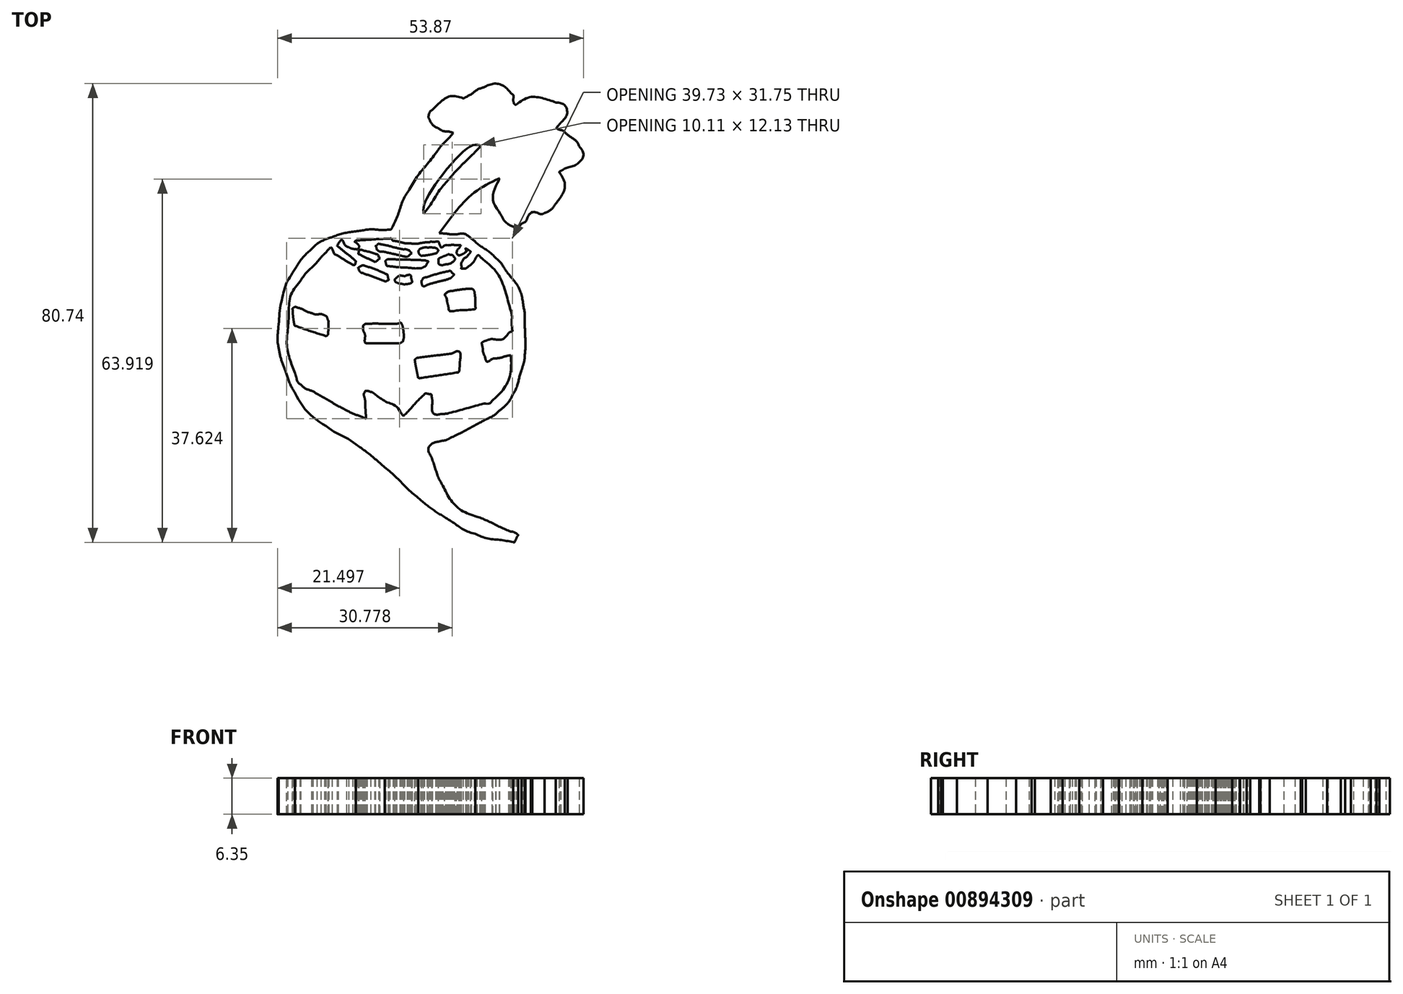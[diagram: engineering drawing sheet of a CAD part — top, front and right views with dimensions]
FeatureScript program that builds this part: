
annotation { "Feature Type Name" : "Feature", "Feature Type Description" : "" }
export const myFeature = defineFeature(function(context is Context, id is Id, definition is map)
    precondition{}
    {
        {
            var Q0;
            Q0=qCreatedBy(makeId("Top.planeOp"),FACE);
            var sketch = newSketch(context, id + "F0", { "sketchPlane" : qUnion([Q0])});
            skFitSpline(sketch, "E0", {"points": [v(4.2, 31.85) * mm, v(3.38, 32.06) * mm, v(2.48, 32.16) * mm, v(1.72, 32.55) * mm]});
            skFitSpline(sketch, "E1", {"points": [v(1.72, 32.55) * mm, v(1.05, 32.89) * mm, v(0.37, 33.47) * mm, v(0.05, 34.12) * mm]});
            skFitSpline(sketch, "E2", {"points": [v(0.05, 34.12) * mm, v(-0.16, 34.54) * mm, v(0.06, 35.5) * mm, v(0.43, 35.84) * mm]});
            skFitSpline(sketch, "E3", {"points": [v(0.43, 35.84) * mm, v(1.95, 37.26) * mm, v(3.7, 38.3) * mm, v(5.93, 37.94) * mm]});
            skFitSpline(sketch, "E4", {"points": [v(5.93, 37.94) * mm, v(6.07, 37.92) * mm, v(6.23, 38.06) * mm, v(6.37, 38.13) * mm]});
            skFitSpline(sketch, "E5", {"points": [v(6.37, 38.13) * mm, v(7.43, 38.71) * mm, v(8.44, 39.44) * mm, v(9.56, 39.85) * mm]});
            skFitSpline(sketch, "E6", {"points": [v(9.56, 39.85) * mm, v(11.38, 40.5) * mm, v(13.1, 40.04) * mm, v(14.48, 38.7) * mm]});
            skFitSpline(sketch, "E7", {"points": [v(14.48, 38.7) * mm, v(14.82, 38.38) * mm, v(14.73, 37.63) * mm, v(14.88, 37.09) * mm]});
            skFitSpline(sketch, "E8", {"points": [v(14.88, 37.09) * mm, v(14.92, 36.96) * mm, v(15.2, 36.77) * mm, v(15.27, 36.8) * mm]});
            skFitSpline(sketch, "E9", {"points": [v(15.27, 36.8) * mm, v(17.56, 38.1) * mm, v(19.92, 37.93) * mm, v(22.3, 37.18) * mm]});
            skFitSpline(sketch, "E10", {"points": [v(22.3, 37.18) * mm, v(23.8, 36.71) * mm, v(24.18, 35.06) * mm, v(23.12, 33.67) * mm]});
            skFitSpline(sketch, "E11", {"points": [v(23.12, 33.67) * mm, v(22.87, 33.34) * mm, v(22.6, 33.03) * mm, v(22.3, 32.68) * mm]});
            skFitSpline(sketch, "E12", {"points": [v(22.3, 32.68) * mm, v(22.85, 32.41) * mm, v(23.45, 32.26) * mm, v(23.9, 31.9) * mm]});
            skFitSpline(sketch, "E13", {"points": [v(23.9, 31.9) * mm, v(24.77, 31.17) * mm, v(25.8, 30.46) * mm, v(26.32, 29.5) * mm]});
            skFitSpline(sketch, "E14", {"points": [v(26.32, 29.5) * mm, v(27.12, 28.07) * mm, v(26.07, 26.4) * mm, v(24.3, 25.73) * mm]});
            skFitSpline(sketch, "E15", {"points": [v(24.3, 25.73) * mm, v(23.84, 25.56) * mm, v(23.4, 25.3) * mm, v(22.97, 25.08) * mm]});
            skFitSpline(sketch, "E16", {"points": [v(22.97, 25.08) * mm, v(22.92, 25.05) * mm, v(22.87, 24.9) * mm, v(22.9, 24.83) * mm]});
            skFitSpline(sketch, "E17", {"points": [v(22.9, 24.83) * mm, v(23.83, 22.88) * mm, v(23.4, 21.04) * mm, v(22.24, 19.39) * mm]});
            skFitSpline(sketch, "E18", {"points": [v(22.24, 19.39) * mm, v(21.76, 18.7) * mm, v(21.01, 18.06) * mm, v(20.25, 17.75) * mm]});
            skFitSpline(sketch, "E19", {"points": [v(20.25, 17.75) * mm, v(19.66, 17.51) * mm, v(18.85, 17.83) * mm, v(18.13, 17.89) * mm]});
            skFitSpline(sketch, "E20", {"points": [v(18.13, 17.89) * mm, v(18.04, 17.9) * mm, v(17.9, 17.82) * mm, v(17.84, 17.75) * mm]});
            skFitSpline(sketch, "E21", {"points": [v(17.84, 17.75) * mm, v(17.34, 17.13) * mm, v(16.98, 16.3) * mm, v(16.34, 15.94) * mm]});
            skFitSpline(sketch, "E22", {"points": [v(16.34, 15.94) * mm, v(15.19, 15.3) * mm, v(13.33, 16.2) * mm, v(12.56, 17.46) * mm, v(11.35, 19.41) * mm, v(11.29, 21.4) * mm, v(12.18, 23.47) * mm]});
            skFitSpline(sketch, "E23", {"points": [v(12.18, 23.47) * mm, v(12.23, 23.57) * mm, v(12.25, 23.67) * mm, v(12.3, 23.84) * mm]});
            skFitSpline(sketch, "E24", {"points": [v(12.3, 23.84) * mm, v(8.03, 21.44) * mm, v(4.7, 18.12) * mm, v(1.72, 14.17) * mm]});
            skFitSpline(sketch, "E25", {"points": [v(1.72, 14.17) * mm, v(2.9, 14.1) * mm, v(3.9, 13.97) * mm, v(4.9, 14.01) * mm]});
            skFitSpline(sketch, "E26", {"points": [v(4.9, 14.01) * mm, v(6.16, 14.07) * mm, v(7.07, 13.5) * mm, v(7.98, 12.76) * mm]});
            skFitSpline(sketch, "E27", {"points": [v(7.98, 12.76) * mm, v(9.19, 11.77) * mm, v(10.52, 10.92) * mm, v(11.64, 9.84) * mm]});
            skFitSpline(sketch, "E28", {"points": [v(11.64, 9.84) * mm, v(12.63, 8.88) * mm, v(13.4, 7.68) * mm, v(14.25, 6.58) * mm]});
            skFitSpline(sketch, "E29", {"points": [v(14.25, 6.58) * mm, v(15.44, 5.05) * mm, v(16.2, 3.3) * mm, v(16.52, 1.4) * mm]});
            skFitSpline(sketch, "E30", {"points": [v(16.52, 1.4) * mm, v(16.77, -0.04) * mm, v(16.78, -1.54) * mm, v(16.82, -3.02) * mm]});
            skFitSpline(sketch, "E31", {"points": [v(16.82, -3.02) * mm, v(16.87, -4.4) * mm, v(16.89, -5.79) * mm, v(16.78, -7.16) * mm]});
            skFitSpline(sketch, "E32", {"points": [v(16.78, -7.16) * mm, v(16.71, -8.11) * mm, v(16.47, -9.06) * mm, v(16.2, -9.98) * mm]});
            skFitSpline(sketch, "E33", {"points": [v(16.2, -9.98) * mm, v(15.76, -11.4) * mm, v(15.38, -12.87) * mm, v(14.69, -14.17) * mm]});
            skFitSpline(sketch, "E34", {"points": [v(14.69, -14.17) * mm, v(14.1, -15.26) * mm, v(13.24, -16.28) * mm, v(12.28, -17.08) * mm]});
            skFitSpline(sketch, "E35", {"points": [v(12.28, -17.08) * mm, v(11.27, -17.94) * mm, v(10.02, -18.55) * mm, v(8.84, -19.19) * mm]});
            skFitSpline(sketch, "E36", {"points": [v(8.84, -19.19) * mm, v(7.07, -20.15) * mm, v(5.27, -21.07) * mm, v(3.46, -21.95) * mm]});
            skFitSpline(sketch, "E37", {"points": [v(3.46, -21.95) * mm, v(2.89, -22.23) * mm, v(2.22, -22.34) * mm, v(1.6, -22.5) * mm]});
            skFitSpline(sketch, "E38", {"points": [v(1.6, -22.5) * mm, v(0.62, -22.77) * mm, v(-0.2, -23.7) * mm, v(0.36, -25.28) * mm]});
            skFitSpline(sketch, "E39", {"points": [v(0.36, -25.28) * mm, v(0.95, -26.96) * mm, v(1.52, -28.69) * mm, v(2.37, -30.25) * mm]});
            skFitSpline(sketch, "E40", {"points": [v(2.37, -30.25) * mm, v(3.71, -32.74) * mm, v(5.69, -34.62) * mm, v(8.39, -35.7) * mm]});
            skFitSpline(sketch, "E41", {"points": [v(8.39, -35.7) * mm, v(10.25, -36.45) * mm, v(12.06, -37.35) * mm, v(13.9, -38.16) * mm]});
            skFitSpline(sketch, "E42", {"points": [v(13.9, -38.16) * mm, v(14.23, -38.3) * mm, v(14.62, -38.33) * mm, v(14.95, -38.48) * mm]});
            skFitSpline(sketch, "E43", {"points": [v(14.95, -38.48) * mm, v(15.2, -38.6) * mm, v(15.61, -38.96) * mm, v(15.6, -39) * mm]});
            skFitSpline(sketch, "E44", {"points": [v(15.6, -39) * mm, v(15.33, -39.43) * mm, v(14.94, -40.21) * mm, v(14.71, -40.17) * mm]});
            skFitSpline(sketch, "E45", {"points": [v(14.71, -40.17) * mm, v(12.47, -39.8) * mm, v(10.17, -39.52) * mm, v(8.06, -38.74) * mm]});
            skFitSpline(sketch, "E46", {"points": [v(8.06, -38.74) * mm, v(6.06, -38) * mm, v(4.23, -36.78) * mm, v(2.4, -35.63) * mm]});
            skFitSpline(sketch, "E47", {"points": [v(2.4, -35.63) * mm, v(0.88, -34.66) * mm, v(-0.6, -33.58) * mm, v(-1.96, -32.4) * mm]});
            skFitSpline(sketch, "E48", {"points": [v(-1.96, -32.4) * mm, v(-3.99, -30.68) * mm, v(-5.86, -28.77) * mm, v(-7.87, -27.02) * mm]});
            skFitSpline(sketch, "E49", {"points": [v(-7.87, -27.02) * mm, v(-9.5, -25.6) * mm, v(-11.18, -24.23) * mm, v(-12.94, -23) * mm]});
            skFitSpline(sketch, "E50", {"points": [v(-12.94, -23) * mm, v(-14.54, -21.87) * mm, v(-16.33, -21.03) * mm, v(-17.94, -19.94) * mm, v(-20.27, -18.35) * mm, v(-22.24, -16.36) * mm, v(-23.66, -13.91) * mm]});
            skFitSpline(sketch, "E51", {"points": [v(-23.66, -13.91) * mm, v(-24.42, -12.6) * mm, v(-24.97, -11.17) * mm, v(-25.5, -9.74) * mm]});
            skFitSpline(sketch, "E52", {"points": [v(-25.5, -9.74) * mm, v(-25.95, -8.5) * mm, v(-26.33, -7.22) * mm, v(-26.55, -5.92) * mm]});
            skFitSpline(sketch, "E53", {"points": [v(-26.55, -5.92) * mm, v(-26.73, -4.9) * mm, v(-26.72, -3.83) * mm, v(-26.63, -2.8) * mm]});
            skFitSpline(sketch, "E54", {"points": [v(-26.63, -2.8) * mm, v(-26.45, -0.88) * mm, v(-26.3, 1.07) * mm, v(-25.87, 2.94) * mm, v(-25.52, 4.4) * mm, v(-24.9, 5.88) * mm, v(-24.12, 7.16) * mm]});
            skFitSpline(sketch, "E55", {"points": [v(-24.12, 7.16) * mm, v(-23.18, 8.69) * mm, v(-22.06, 10.16) * mm, v(-20.76, 11.38) * mm]});
            skFitSpline(sketch, "E56", {"points": [v(-20.76, 11.38) * mm, v(-19.76, 12.32) * mm, v(-18.44, 13.05) * mm, v(-17.14, 13.5) * mm]});
            skFitSpline(sketch, "E57", {"points": [v(-17.14, 13.5) * mm, v(-15.43, 14.1) * mm, v(-13.6, 14.44) * mm, v(-11.8, 14.67) * mm]});
            skFitSpline(sketch, "E58", {"points": [v(-11.8, 14.67) * mm, v(-10.21, 14.87) * mm, v(-8.59, 14.75) * mm, v(-6.98, 14.83) * mm]});
            skFitSpline(sketch, "E59", {"points": [v(-6.98, 14.83) * mm, v(-6.78, 14.84) * mm, v(-6.55, 15.22) * mm, v(-6.43, 15.48) * mm]});
            skFitSpline(sketch, "E60", {"points": [v(-6.43, 15.48) * mm, v(-5.47, 17.6) * mm, v(-4.73, 19.86) * mm, v(-3.54, 21.84) * mm]});
            skFitSpline(sketch, "E61", {"points": [v(-3.54, 21.84) * mm, v(-2.08, 24.26) * mm, v(-0.28, 26.47) * mm, v(1.44, 28.72) * mm]});
            skFitSpline(sketch, "E62", {"points": [v(1.44, 28.72) * mm, v(2.28, 29.82) * mm, v(3.28, 30.81) * mm, v(4.2, 31.85) * mm]});
            skFitSpline(sketch, "E63", {"points": [v(5.54, 12.07) * mm, v(4.84, 12.07) * mm, v(4.03, 12.12) * mm, v(3.24, 12.05) * mm]});
            skFitSpline(sketch, "E64", {"points": [v(3.24, 12.05) * mm, v(2.65, 12) * mm, v(2.1, 11.66) * mm, v(1.7, 12.48) * mm]});
            skFitSpline(sketch, "E65", {"points": [v(1.7, 12.48) * mm, v(1.57, 12.72) * mm, v(0.82, 12.64) * mm, v(0.36, 12.7) * mm]});
            skFitSpline(sketch, "E66", {"points": [v(0.36, 12.7) * mm, v(0.22, 12.7) * mm, v(0.08, 12.63) * mm, v(-0.07, 12.62) * mm]});
            skFitSpline(sketch, "E67", {"points": [v(-0.07, 12.62) * mm, v(-1.12, 12.53) * mm, v(-2.18, 12.34) * mm, v(-3.23, 12.38) * mm]});
            skFitSpline(sketch, "E68", {"points": [v(-3.23, 12.38) * mm, v(-4.24, 12.41) * mm, v(-5.25, 12.65) * mm, v(-6.25, 12.85) * mm]});
            skFitSpline(sketch, "E69", {"points": [v(-6.25, 12.85) * mm, v(-6.5, 12.9) * mm, v(-6.73, 13.25) * mm, v(-6.96, 13.24) * mm]});
            skFitSpline(sketch, "E70", {"points": [v(-6.96, 13.24) * mm, v(-8.92, 13.16) * mm, v(-10.89, 13.02) * mm, v(-12.85, 12.9) * mm]});
            skFitSpline(sketch, "E71", {"points": [v(-12.85, 12.9) * mm, v(-12.96, 12.89) * mm, v(-13.07, 12.8) * mm, v(-13.23, 12.72) * mm]});
            skFitSpline(sketch, "E72", {"points": [v(-13.23, 12.72) * mm, v(-13.04, 12.6) * mm, v(-12.9, 12.56) * mm, v(-12.8, 12.46) * mm]});
            skFitSpline(sketch, "E73", {"points": [v(-12.8, 12.46) * mm, v(-12.64, 12.26) * mm, v(-12.42, 12.04) * mm, v(-12.41, 11.82) * mm]});
            skFitSpline(sketch, "E74", {"points": [v(-12.41, 11.82) * mm, v(-12.4, 11.67) * mm, v(-12.72, 11.35) * mm, v(-12.87, 11.37) * mm]});
            skFitSpline(sketch, "E75", {"points": [v(-12.87, 11.37) * mm, v(-13.32, 11.41) * mm, v(-13.8, 11.51) * mm, v(-14.2, 11.72) * mm]});
            skFitSpline(sketch, "E76", {"points": [v(-14.2, 11.72) * mm, v(-14.86, 12.07) * mm, v(-15.4, 13) * mm, v(-16.25, 11.94) * mm]});
            skFitSpline(sketch, "E77", {"points": [v(-16.25, 11.94) * mm, v(-16.22, 11.92) * mm, v(-16.15, 11.89) * mm, v(-16.1, 11.84) * mm]});
            skFitSpline(sketch, "E78", {"points": [v(-16.1, 11.84) * mm, v(-15.09, 11.02) * mm, v(-14.08, 10.22) * mm, v(-13.1, 9.37) * mm]});
            skFitSpline(sketch, "E79", {"points": [v(-13.1, 9.37) * mm, v(-12.98, 9.27) * mm, v(-13.03, 8.93) * mm, v(-13.08, 8.72) * mm]});
            skFitSpline(sketch, "E80", {"points": [v(-13.08, 8.72) * mm, v(-13.1, 8.66) * mm, v(-13.42, 8.57) * mm, v(-13.52, 8.63) * mm]});
            skFitSpline(sketch, "E81", {"points": [v(-13.52, 8.63) * mm, v(-14.4, 9.15) * mm, v(-15.28, 9.7) * mm, v(-16.15, 10.24) * mm]});
            skFitSpline(sketch, "E82", {"points": [v(-16.15, 10.24) * mm, v(-16.8, 10.65) * mm, v(-17.28, 11.66) * mm, v(-18.25, 10.77) * mm]});
            skFitSpline(sketch, "E83", {"points": [v(-18.25, 10.77) * mm, v(-18.55, 10.5) * mm, v(-18.84, 10.21) * mm, v(-19.11, 9.9) * mm]});
            skFitSpline(sketch, "E84", {"points": [v(-19.11, 9.9) * mm, v(-20.35, 8.5) * mm, v(-21.72, 7.18) * mm, v(-22.77, 5.65) * mm]});
            skFitSpline(sketch, "E85", {"points": [v(-22.77, 5.65) * mm, v(-24.47, 3.12) * mm, v(-24.75, 0.12) * mm, v(-24.94, -2.82) * mm]});
            skFitSpline(sketch, "E86", {"points": [v(-24.94, -2.82) * mm, v(-25.1, -5.4) * mm, v(-24.59, -7.93) * mm, v(-23.72, -10.37) * mm]});
            skFitSpline(sketch, "E87", {"points": [v(-23.72, -10.37) * mm, v(-23.45, -11.1) * mm, v(-23.2, -11.97) * mm, v(-22.65, -12.44) * mm]});
            skFitSpline(sketch, "E88", {"points": [v(-22.65, -12.44) * mm, v(-21.83, -13.15) * mm, v(-20.76, -13.56) * mm, v(-19.8, -14.1) * mm]});
            skFitSpline(sketch, "E89", {"points": [v(-19.8, -14.1) * mm, v(-18.07, -15.06) * mm, v(-16.36, -16.07) * mm, v(-14.61, -16.98) * mm]});
            skFitSpline(sketch, "E90", {"points": [v(-14.61, -16.98) * mm, v(-13.5, -17.55) * mm, v(-12.33, -17.97) * mm, v(-11.14, -18.48) * mm]});
            skFitSpline(sketch, "E91", {"points": [v(-11.14, -18.48) * mm, v(-11.18, -17.85) * mm, v(-11.23, -17.26) * mm, v(-11.27, -16.68) * mm]});
            skFitSpline(sketch, "E92", {"points": [v(-11.27, -16.68) * mm, v(-11.31, -16.1) * mm, v(-11.3, -15.5) * mm, v(-11.4, -14.92) * mm]});
            skFitSpline(sketch, "E93", {"points": [v(-11.4, -14.92) * mm, v(-11.53, -14.06) * mm, v(-11.2, -13.57) * mm, v(-10.34, -13.75) * mm]});
            skFitSpline(sketch, "E94", {"points": [v(-10.34, -13.75) * mm, v(-10.09, -13.8) * mm, v(-9.85, -13.95) * mm, v(-9.62, -14.13) * mm]});
            skFitSpline(sketch, "E95", {"points": [v(-9.62, -14.13) * mm, v(-9.39, -14.3) * mm, v(-9.16, -14.5) * mm, v(-8.92, -14.66) * mm]});
            skFitSpline(sketch, "E96", {"points": [v(-8.92, -14.66) * mm, v(-7.42, -15.56) * mm, v(-5.84, -16.34) * mm, v(-4.79, -17.83) * mm, v(-4.75, -17.89) * mm, v(-4.45, -17.86) * mm, v(-4.37, -17.78) * mm]});
            skFitSpline(sketch, "E97", {"points": [v(-4.37, -17.78) * mm, v(-3.24, -16.6) * mm, v(-2.15, -15.38) * mm, v(-0.97, -14.25) * mm]});
            skFitSpline(sketch, "E98", {"points": [v(-0.97, -14.25) * mm, v(-0.74, -14.03) * mm, v(-0.18, -14.1) * mm, v(0.2, -14.15) * mm]});
            skFitSpline(sketch, "E99", {"points": [v(0.2, -14.15) * mm, v(0.31, -14.16) * mm, v(0.4, -14.6) * mm, v(0.44, -14.85) * mm]});
            skFitSpline(sketch, "E100", {"points": [v(0.44, -14.85) * mm, v(0.49, -15.13) * mm, v(0.5, -15.42) * mm, v(0.5, -15.7) * mm]});
            skFitSpline(sketch, "E101", {"points": [v(0.5, -15.7) * mm, v(0.47, -17.12) * mm, v(0.94, -17.7) * mm, v(2.13, -17.63) * mm]});
            skFitSpline(sketch, "E102", {"points": [v(2.13, -17.63) * mm, v(2.57, -17.6) * mm, v(3.01, -17.58) * mm, v(3.43, -17.47) * mm]});
            skFitSpline(sketch, "E103", {"points": [v(3.43, -17.47) * mm, v(5.25, -17) * mm, v(7.06, -16.5) * mm, v(8.86, -16) * mm, v(9.58, -15.8) * mm, v(10.51, -15.8) * mm, v(10.96, -15.34) * mm]});
            skFitSpline(sketch, "E104", {"points": [v(10.96, -15.34) * mm, v(13.1, -13.18) * mm, v(14.25, -10.52) * mm, v(14.36, -7.46) * mm]});
            skFitSpline(sketch, "E105", {"points": [v(14.36, -7.46) * mm, v(14.36, -7.41) * mm, v(14.2, -7.3) * mm, v(14.13, -7.32) * mm]});
            skFitSpline(sketch, "E106", {"points": [v(14.13, -7.32) * mm, v(13.31, -7.5) * mm, v(12.5, -7.74) * mm, v(11.68, -7.85) * mm]});
            skFitSpline(sketch, "E107", {"points": [v(11.68, -7.85) * mm, v(11.02, -7.93) * mm, v(10.17, -8.46) * mm, v(9.76, -7.5) * mm]});
            skFitSpline(sketch, "E108", {"points": [v(9.76, -7.5) * mm, v(9.46, -6.8) * mm, v(9.36, -6) * mm, v(9.2, -5.23) * mm]});
            skFitSpline(sketch, "E109", {"points": [v(9.2, -5.23) * mm, v(9.2, -5.15) * mm, v(9.37, -4.97) * mm, v(9.5, -4.93) * mm]});
            skFitSpline(sketch, "E110", {"points": [v(9.5, -4.93) * mm, v(10.98, -4.45) * mm, v(12.66, -4.54) * mm, v(13.93, -3.41) * mm]});
            skFitSpline(sketch, "E111", {"points": [v(13.93, -3.41) * mm, v(14.14, -3.23) * mm, v(14.6, -3.07) * mm, v(14.58, -2.92) * mm]});
            skFitSpline(sketch, "E112", {"points": [v(14.58, -2.92) * mm, v(14.49, -1.57) * mm, v(14.5, -0.18) * mm, v(14.13, 1.1) * mm]});
            skFitSpline(sketch, "E113", {"points": [v(14.13, 1.1) * mm, v(13.25, 4.27) * mm, v(11.9, 7.22) * mm, v(9.46, 9.56) * mm]});
            skFitSpline(sketch, "E114", {"points": [v(9.46, 9.56) * mm, v(8.92, 10.08) * mm, v(8.55, 10.33) * mm, v(8.01, 9.53) * mm]});
            skFitSpline(sketch, "E115", {"points": [v(8.01, 9.53) * mm, v(7.65, 8.98) * mm, v(7.13, 8.52) * mm, v(6.6, 8.12) * mm]});
            skFitSpline(sketch, "E116", {"points": [v(6.6, 8.12) * mm, v(6.35, 7.93) * mm, v(5.92, 7.98) * mm, v(5.57, 7.92) * mm]});
            skFitSpline(sketch, "E117", {"points": [v(5.57, 7.92) * mm, v(5.64, 8.37) * mm, v(5.6, 8.9) * mm, v(5.8, 9.27) * mm, v(6.05, 9.71) * mm, v(6.53, 10.02) * mm, v(6.89, 10.4) * mm]});
            skFitSpline(sketch, "E118", {"points": [v(6.89, 10.4) * mm, v(7.04, 10.58) * mm, v(7.25, 10.95) * mm, v(7.23, 10.97) * mm]});
            skFitSpline(sketch, "E119", {"points": [v(7.23, 10.97) * mm, v(6.93, 11.2) * mm, v(6.6, 11.4) * mm, v(6.34, 11.56) * mm]});
            skFitSpline(sketch, "E120", {"points": [v(6.34, 11.56) * mm, v(6.39, 11.33) * mm, v(6.53, 10.97) * mm, v(6.46, 10.92) * mm]});
            skFitSpline(sketch, "E121", {"points": [v(6.46, 10.92) * mm, v(6.08, 10.66) * mm, v(5.66, 10.43) * mm, v(5.23, 10.28) * mm]});
            skFitSpline(sketch, "E122", {"points": [v(5.23, 10.28) * mm, v(5.16, 10.26) * mm, v(4.77, 10.73) * mm, v(4.81, 10.89) * mm]});
            skFitSpline(sketch, "E123", {"points": [v(4.81, 10.89) * mm, v(4.92, 11.25) * mm, v(5.2, 11.55) * mm, v(5.54, 12.07) * mm]});
            skFitSpline(sketch, "E124", {"points": [v(-1, 17.62) * mm, v(0.45, 19.64) * mm, v(1.86, 21.85) * mm, v(3.54, 23.84) * mm]});
            skFitSpline(sketch, "E125", {"points": [v(3.54, 23.84) * mm, v(4.38, 24.83) * mm, v(5.3, 25.78) * mm, v(6.23, 26.71) * mm]});
            skFitSpline(sketch, "E126", {"points": [v(6.23, 26.71) * mm, v(7.17, 27.64) * mm, v(8.13, 28.57) * mm, v(9.08, 29.54) * mm]});
            skFitSpline(sketch, "E127", {"points": [v(9.08, 29.54) * mm, v(7.17, 29.46) * mm, v(-0.59, 20.08) * mm, v(-1, 17.62) * mm]});
            skFitSpline(sketch, "E128", {"points": [v(5.39, -8.12) * mm, v(5.34, -8.77) * mm, v(5.3, -9.42) * mm, v(5.23, -10.06) * mm]});
            skFitSpline(sketch, "E129", {"points": [v(5.23, -10.06) * mm, v(5.22, -10.16) * mm, v(5.08, -10.3) * mm, v(4.98, -10.32) * mm]});
            skFitSpline(sketch, "E130", {"points": [v(4.98, -10.32) * mm, v(2.8, -10.66) * mm, v(0.6, -11) * mm, v(-1.59, -11.3) * mm]});
            skFitSpline(sketch, "E131", {"points": [v(-1.59, -11.3) * mm, v(-1.72, -11.33) * mm, v(-1.99, -11.23) * mm, v(-2, -11.14) * mm]});
            skFitSpline(sketch, "E132", {"points": [v(-2, -11.14) * mm, v(-2.11, -10.66) * mm, v(-2.22, -10.17) * mm, v(-2.31, -9.68) * mm]});
            skFitSpline(sketch, "E133", {"points": [v(-2.31, -9.68) * mm, v(-2.4, -9.19) * mm, v(-2.5, -8.7) * mm, v(-2.56, -8.2) * mm]});
            skFitSpline(sketch, "E134", {"points": [v(-2.56, -8.2) * mm, v(-2.57, -8.07) * mm, v(-2.17, -7.76) * mm, v(-1.93, -7.73) * mm]});
            skFitSpline(sketch, "E135", {"points": [v(-1.93, -7.73) * mm, v(-0.02, -7.47) * mm, v(1.9, -7.25) * mm, v(3.8, -7.02) * mm]});
            skFitSpline(sketch, "E136", {"points": [v(3.8, -7.02) * mm, v(3.86, -7) * mm, v(3.92, -6.99) * mm, v(3.98, -6.97) * mm]});
            skFitSpline(sketch, "E137", {"points": [v(3.98, -6.97) * mm, v(5, -6.59) * mm, v(5.43, -6.95) * mm, v(5.39, -8.12) * mm]});
            skFitSpline(sketch, "E138", {"points": [v(-5.13, -5.18) * mm, v(-6.97, -5.18) * mm, v(-8.55, -5.16) * mm, v(-10.13, -5.2) * mm]});
            skFitSpline(sketch, "E139", {"points": [v(-10.13, -5.2) * mm, v(-10.85, -5.2) * mm, v(-11.32, -5.1) * mm, v(-11.35, -4.22) * mm]});
            skFitSpline(sketch, "E140", {"points": [v(-11.35, -4.22) * mm, v(-11.37, -3.58) * mm, v(-11.65, -2.96) * mm, v(-11.68, -2.32) * mm]});
            skFitSpline(sketch, "E141", {"points": [v(-11.68, -2.32) * mm, v(-11.69, -2.14) * mm, v(-11.25, -1.76) * mm, v(-11, -1.75) * mm]});
            skFitSpline(sketch, "E142", {"points": [v(-11, -1.75) * mm, v(-9.37, -1.72) * mm, v(-7.73, -1.76) * mm, v(-6.08, -1.78) * mm]});
            skFitSpline(sketch, "E143", {"points": [v(-6.08, -1.78) * mm, v(-6.05, -1.78) * mm, v(-6.03, -1.78) * mm, v(-6, -1.78) * mm]});
            skFitSpline(sketch, "E144", {"points": [v(-6, -1.78) * mm, v(-5.63, -1.74) * mm, v(-5, -1.58) * mm, v(-4.95, -1.69) * mm]});
            skFitSpline(sketch, "E145", {"points": [v(-4.95, -1.69) * mm, v(-4.73, -2.15) * mm, v(-4.62, -2.7) * mm, v(-4.56, -3.23) * mm]});
            skFitSpline(sketch, "E146", {"points": [v(-4.56, -3.23) * mm, v(-4.51, -3.7) * mm, v(-4.52, -4.19) * mm, v(-4.64, -4.64) * mm]});
            skFitSpline(sketch, "E147", {"points": [v(-4.64, -4.64) * mm, v(-4.7, -4.89) * mm, v(-5.02, -5.07) * mm, v(-5.13, -5.18) * mm]});
            skFitSpline(sketch, "E148", {"points": [v(-17.74, -1.25) * mm, v(-17.8, -2.22) * mm, v(-17.8, -2.9) * mm, v(-17.87, -3.55) * mm]});
            skFitSpline(sketch, "E149", {"points": [v(-17.87, -3.55) * mm, v(-17.89, -3.69) * mm, v(-18.2, -3.92) * mm, v(-18.3, -3.9) * mm]});
            skFitSpline(sketch, "E150", {"points": [v(-18.3, -3.9) * mm, v(-20.05, -3.34) * mm, v(-21.8, -2.76) * mm, v(-23.52, -2.15) * mm]});
            skFitSpline(sketch, "E151", {"points": [v(-23.52, -2.15) * mm, v(-23.7, -2.1) * mm, v(-23.82, -1.75) * mm, v(-23.85, -1.53) * mm]});
            skFitSpline(sketch, "E152", {"points": [v(-23.85, -1.53) * mm, v(-23.91, -1.15) * mm, v(-23.97, -0.76) * mm, v(-24.01, -0.38) * mm]});
            skFitSpline(sketch, "E153", {"points": [v(-24.01, -0.38) * mm, v(-24.06, 0) * mm, v(-24.09, 0.4) * mm, v(-24.1, 0.78) * mm]});
            skFitSpline(sketch, "E154", {"points": [v(-24.1, 0.78) * mm, v(-24.1, 0.91) * mm, v(-23.64, 1.23) * mm, v(-23.48, 1.17) * mm]});
            skFitSpline(sketch, "E155", {"points": [v(-23.48, 1.17) * mm, v(-22.48, 0.84) * mm, v(-21.52, 0.38) * mm, v(-20.52, 0.06) * mm]});
            skFitSpline(sketch, "E156", {"points": [v(-20.52, 0.06) * mm, v(-19.86, -0.14) * mm, v(-19.1, -0.04) * mm, v(-18.48, -0.3) * mm]});
            skFitSpline(sketch, "E157", {"points": [v(-18.48, -0.3) * mm, v(-18.1, -0.46) * mm, v(-17.9, -1.04) * mm, v(-17.74, -1.25) * mm]});
            skFitSpline(sketch, "E158", {"points": [v(3.1, 2.3) * mm, v(3, 2.73) * mm, v(2.7, 3.43) * mm, v(2.86, 3.57) * mm, v(3.25, 3.89) * mm, v(3.84, 4.01) * mm, v(4.38, 4.1) * mm]});
            skFitSpline(sketch, "E159", {"points": [v(4.38, 4.1) * mm, v(5.36, 4.25) * mm, v(6.35, 4.37) * mm, v(7.35, 4.4) * mm]});
            skFitSpline(sketch, "E160", {"points": [v(7.35, 4.4) * mm, v(7.55, 4.4) * mm, v(7.9, 3.94) * mm, v(7.94, 3.66) * mm]});
            skFitSpline(sketch, "E161", {"points": [v(7.94, 3.66) * mm, v(8.07, 2.78) * mm, v(8.08, 1.89) * mm, v(8.1, 1) * mm]});
            skFitSpline(sketch, "E162", {"points": [v(8.1, 1) * mm, v(8.1, 0.92) * mm, v(7.9, 0.77) * mm, v(7.79, 0.76) * mm, v(6.64, 0.67) * mm, v(5.48, 0.65) * mm, v(4.34, 0.5) * mm, v(3.77, 0.43) * mm, v(3.47, 0.53) * mm, v(3.35, 1.1) * mm]});
            skFitSpline(sketch, "E163", {"points": [v(3.35, 1.1) * mm, v(3.27, 1.5) * mm, v(3.16, 1.89) * mm, v(3.06, 2.29) * mm]});
            skFitSpline(sketch, "E164", {"points": [v(3.06, 2.29) * mm, v(3.07, 2.29) * mm, v(3.08, 2.29) * mm, v(3.1, 2.3) * mm]});
            skFitSpline(sketch, "E165", {"points": [v(-2.35, 7.99) * mm, v(-4.16, 8.13) * mm, v(-5.74, 8.23) * mm, v(-7.31, 8.42) * mm]});
            skFitSpline(sketch, "E166", {"points": [v(-7.31, 8.42) * mm, v(-7.5, 8.44) * mm, v(-7.68, 8.93) * mm, v(-7.75, 9.23) * mm]});
            skFitSpline(sketch, "E167", {"points": [v(-7.75, 9.23) * mm, v(-7.77, 9.3) * mm, v(-7.33, 9.6) * mm, v(-7.1, 9.59) * mm]});
            skFitSpline(sketch, "E168", {"points": [v(-7.1, 9.59) * mm, v(-6.12, 9.58) * mm, v(-5.14, 9.56) * mm, v(-4.15, 9.53) * mm]});
            skFitSpline(sketch, "E169", {"points": [v(-4.15, 9.53) * mm, v(-3.16, 9.5) * mm, v(-2.18, 9.47) * mm, v(-1.2, 9.44) * mm]});
            skFitSpline(sketch, "E170", {"points": [v(-1.2, 9.44) * mm, v(-0.84, 9.42) * mm, v(-0.49, 9.3) * mm, v(-0.14, 9.23) * mm]});
            skFitSpline(sketch, "E171", {"points": [v(-0.14, 9.23) * mm, v(-0.42, 8.9) * mm, v(-0.63, 8.43) * mm, v(-0.99, 8.26) * mm]});
            skFitSpline(sketch, "E172", {"points": [v(-0.99, 8.26) * mm, v(-1.45, 8.03) * mm, v(-2.03, 8.04) * mm, v(-2.35, 7.99) * mm]});
            skFitSpline(sketch, "E173", {"points": [v(-3.93, 9.98) * mm, v(-5.33, 10.3) * mm, v(-6.62, 10.6) * mm, v(-7.91, 10.89) * mm]});
            skFitSpline(sketch, "E174", {"points": [v(-7.91, 10.89) * mm, v(-8.27, 10.97) * mm, v(-8.69, 10.92) * mm, v(-8.98, 11.1) * mm]});
            skFitSpline(sketch, "E175", {"points": [v(-8.98, 11.1) * mm, v(-9.23, 11.25) * mm, v(-9.33, 11.64) * mm, v(-9.5, 11.92) * mm]});
            skFitSpline(sketch, "E176", {"points": [v(-9.5, 11.92) * mm, v(-9.27, 12.05) * mm, v(-9.01, 12.33) * mm, v(-8.81, 12.29) * mm]});
            skFitSpline(sketch, "E177", {"points": [v(-8.81, 12.29) * mm, v(-7.55, 12.04) * mm, v(-6.3, 11.72) * mm, v(-5.04, 11.44) * mm]});
            skFitSpline(sketch, "E178", {"points": [v(-5.04, 11.44) * mm, v(-4.63, 11.34) * mm, v(-4.18, 11.35) * mm, v(-3.78, 11.22) * mm]});
            skFitSpline(sketch, "E179", {"points": [v(-3.78, 11.22) * mm, v(-3.53, 11.14) * mm, v(-3.35, 10.88) * mm, v(-3.13, 10.7) * mm]});
            skFitSpline(sketch, "E180", {"points": [v(-3.13, 10.7) * mm, v(-3.4, 10.47) * mm, v(-3.66, 10.23) * mm, v(-3.93, 9.98) * mm]});
            skFitSpline(sketch, "E181", {"points": [v(-1.37, 5.85) * mm, v(-1.27, 5.96) * mm, v(-1.11, 6.28) * mm, v(-0.88, 6.35) * mm]});
            skFitSpline(sketch, "E182", {"points": [v(-0.88, 6.35) * mm, v(0.53, 6.78) * mm, v(1.94, 7.2) * mm, v(3.37, 7.5) * mm]});
            skFitSpline(sketch, "E183", {"points": [v(3.37, 7.5) * mm, v(3.66, 7.56) * mm, v(4.05, 7.14) * mm, v(4.4, 6.94) * mm]});
            skFitSpline(sketch, "E184", {"points": [v(4.4, 6.94) * mm, v(4.26, 6.82) * mm, v(4.14, 6.66) * mm, v(4.01, 6.53) * mm]});
            skFitSpline(sketch, "E185", {"points": [v(4.01, 6.53) * mm, v(3.88, 6.4) * mm, v(3.75, 6.27) * mm, v(3.6, 6.22) * mm]});
            skFitSpline(sketch, "E186", {"points": [v(3.6, 6.22) * mm, v(2.54, 5.88) * mm, v(1.46, 5.63) * mm, v(0.39, 5.34) * mm]});
            skFitSpline(sketch, "E187", {"points": [v(0.39, 5.34) * mm, v(0.1, 5.26) * mm, v(-0.19, 5.16) * mm, v(-0.47, 5.05) * mm]});
            skFitSpline(sketch, "E188", {"points": [v(-0.47, 5.05) * mm, v(-1.05, 4.83) * mm, v(-1.31, 5.08) * mm, v(-1.37, 5.85) * mm]});
            skFitSpline(sketch, "E189", {"points": [v(-7.68, 5.69) * mm, v(-8.97, 6.16) * mm, v(-10.25, 6.62) * mm, v(-11.52, 7.1) * mm]});
            skFitSpline(sketch, "E190", {"points": [v(-11.52, 7.1) * mm, v(-11.75, 7.18) * mm, v(-12.03, 7.24) * mm, v(-12.2, 7.4) * mm]});
            skFitSpline(sketch, "E191", {"points": [v(-12.2, 7.4) * mm, v(-12.38, 7.6) * mm, v(-12.46, 7.88) * mm, v(-12.58, 8.12) * mm]});
            skFitSpline(sketch, "E192", {"points": [v(-12.58, 8.12) * mm, v(-12.41, 8.2) * mm, v(-12.23, 8.31) * mm, v(-12.05, 8.4) * mm]});
            skFitSpline(sketch, "E193", {"points": [v(-12.05, 8.4) * mm, v(-11.87, 8.5) * mm, v(-11.7, 8.56) * mm, v(-11.57, 8.52) * mm]});
            skFitSpline(sketch, "E194", {"points": [v(-11.57, 8.52) * mm, v(-10.25, 8.08) * mm, v(-8.94, 7.58) * mm, v(-7.67, 7) * mm]});
            skFitSpline(sketch, "E195", {"points": [v(-7.67, 7) * mm, v(-7.4, 6.89) * mm, v(-7.3, 6.37) * mm, v(-7.17, 6.01) * mm]});
            skFitSpline(sketch, "E196", {"points": [v(-7.17, 6.01) * mm, v(-7.15, 5.98) * mm, v(-7.46, 5.82) * mm, v(-7.68, 5.69) * mm]});
            skFitSpline(sketch, "E197", {"points": [v(-9.55, 9.12) * mm, v(-10.54, 9.59) * mm, v(-11.48, 10) * mm, v(-12.38, 10.47) * mm]});
            skFitSpline(sketch, "E198", {"points": [v(-12.38, 10.47) * mm, v(-12.48, 10.53) * mm, v(-12.45, 10.92) * mm, v(-12.4, 11.14) * mm]});
            skFitSpline(sketch, "E199", {"points": [v(-12.4, 11.14) * mm, v(-12.38, 11.2) * mm, v(-12.1, 11.27) * mm, v(-11.96, 11.23) * mm]});
            skFitSpline(sketch, "E200", {"points": [v(-11.96, 11.23) * mm, v(-11.08, 11.01) * mm, v(-10.2, 10.8) * mm, v(-9.34, 10.5) * mm, v(-9.08, 10.4) * mm, v(-8.91, 10.03) * mm, v(-8.7, 9.79) * mm]});
            skFitSpline(sketch, "E201", {"points": [v(-8.7, 9.79) * mm, v(-8.96, 9.59) * mm, v(-9.21, 9.39) * mm, v(-9.55, 9.12) * mm]});
            skFitSpline(sketch, "E202", {"points": [v(0.28, 11.71) * mm, v(0.6, 11.66) * mm, v(0.91, 11.64) * mm, v(1.19, 11.54) * mm]});
            skFitSpline(sketch, "E203", {"points": [v(1.19, 11.54) * mm, v(1.35, 11.47) * mm, v(1.47, 11.27) * mm, v(1.6, 11.13) * mm]});
            skFitSpline(sketch, "E204", {"points": [v(1.6, 11.13) * mm, v(1.43, 10.96) * mm, v(1.27, 10.67) * mm, v(1.06, 10.62) * mm]});
            skFitSpline(sketch, "E205", {"points": [v(1.06, 10.62) * mm, v(0.68, 10.53) * mm, v(0.3, 10.44) * mm, v(-0.08, 10.37) * mm]});
            skFitSpline(sketch, "E206", {"points": [v(-0.08, 10.37) * mm, v(-0.46, 10.3) * mm, v(-0.85, 10.25) * mm, v(-1.23, 10.23) * mm]});
            skFitSpline(sketch, "E207", {"points": [v(-1.23, 10.23) * mm, v(-1.46, 10.22) * mm, v(-1.85, 10.6) * mm, v(-1.9, 10.84) * mm]});
            skFitSpline(sketch, "E208", {"points": [v(-1.9, 10.84) * mm, v(-1.93, 11.04) * mm, v(-1.61, 11.47) * mm, v(-1.38, 11.54) * mm]});
            skFitSpline(sketch, "E209", {"points": [v(-1.38, 11.54) * mm, v(-0.84, 11.68) * mm, v(-0.26, 11.67) * mm, v(0.28, 11.71) * mm]});
            skFitSpline(sketch, "E210", {"points": [v(-4.42, 5.16) * mm, v(-4.83, 5.26) * mm, v(-5.34, 5.34) * mm, v(-5.8, 5.53) * mm]});
            skFitSpline(sketch, "E211", {"points": [v(-5.8, 5.53) * mm, v(-5.95, 5.59) * mm, v(-6.12, 6.04) * mm, v(-6.07, 6.1) * mm]});
            skFitSpline(sketch, "E212", {"points": [v(-6.07, 6.1) * mm, v(-5.82, 6.35) * mm, v(-5.51, 6.6) * mm, v(-5.18, 6.7) * mm]});
            skFitSpline(sketch, "E213", {"points": [v(-5.18, 6.7) * mm, v(-5.04, 6.74) * mm, v(-4.88, 6.71) * mm, v(-4.71, 6.68) * mm]});
            skFitSpline(sketch, "E214", {"points": [v(-4.71, 6.68) * mm, v(-4.55, 6.65) * mm, v(-4.39, 6.62) * mm, v(-4.24, 6.65) * mm, v(-3.41, 6.85) * mm, v(-3.21, 6.32) * mm, v(-3.07, 5.73) * mm]});
            skFitSpline(sketch, "E215", {"points": [v(-3.07, 5.73) * mm, v(-3.04, 5.63) * mm, v(-3.2, 5.42) * mm, v(-3.33, 5.38) * mm]});
            skFitSpline(sketch, "E216", {"points": [v(-3.33, 5.38) * mm, v(-3.65, 5.28) * mm, v(-3.99, 5.24) * mm, v(-4.42, 5.16) * mm]});
            skFitSpline(sketch, "E217", {"points": [v(3.4, 10.5) * mm, v(3.64, 10.39) * mm, v(4.07, 10.31) * mm, v(4.23, 10.06) * mm]});
            skFitSpline(sketch, "E218", {"points": [v(4.23, 10.06) * mm, v(4.52, 9.62) * mm, v(3.7, 8.88) * mm, v(2.82, 8.69) * mm]});
            skFitSpline(sketch, "E219", {"points": [v(2.82, 8.69) * mm, v(2.52, 8.62) * mm, v(2.23, 8.55) * mm, v(2, 8.6) * mm]});
            skFitSpline(sketch, "E220", {"points": [v(2, 8.6) * mm, v(1.77, 8.66) * mm, v(1.6, 8.84) * mm, v(1.57, 9.3) * mm]});
            skFitSpline(sketch, "E221", {"points": [v(1.57, 9.3) * mm, v(1.56, 9.45) * mm, v(1.62, 9.7) * mm, v(1.72, 9.76) * mm]});
            skFitSpline(sketch, "E222", {"points": [v(1.72, 9.76) * mm, v(2.23, 10.02) * mm, v(2.77, 10.23) * mm, v(3.4, 10.5) * mm]});
            skLineSegment(sketch, "E223.bottom", {"start": v(-30.8, 55.45) * mm, "end": v(32.7, 55.45) * mm});
            skLineSegment(sketch, "E223.top", {"start": v(-30.8, -46.15) * mm, "end": v(32.7, -46.15) * mm});
            skLineSegment(sketch, "E223.left", {"start": v(-30.8, 55.45) * mm, "end": v(-30.8, -46.15) * mm});
            skLineSegment(sketch, "E223.right", {"start": v(32.7, 55.45) * mm, "end": v(32.7, -46.15) * mm});
            skSolve(sketch);
        }
        {
            var Q0;
            Q0=makeQuery(id+"F0.imprint","IMPRINT",FACE,{"disambiguationData":[TD([[makeQuery(id+"F0.imprint","IMPRINT",EDGE,{"derivedFrom":sQuery(id+"F0.wireOp",EDGE,"E0")}),-1.0]])]});
            var Q1;
            Q1=makeQuery(id+"F0.imprint","IMPRINT",FACE,{"disambiguationData":[TD([[makeQuery(id+"F0.imprint","IMPRINT",EDGE,{"derivedFrom":sQuery(id+"F0.wireOp",EDGE,"E128")}),-1.0]])]});
            var Q2;
            Q2=makeQuery(id+"F0.imprint","IMPRINT",FACE,{"disambiguationData":[TD([[makeQuery(id+"F0.imprint","IMPRINT",EDGE,{"derivedFrom":sQuery(id+"F0.wireOp",EDGE,"E138")}),-1.0]])]});
            var Q3;
            Q3=makeQuery(id+"F0.imprint","IMPRINT",FACE,{"disambiguationData":[TD([[makeQuery(id+"F0.imprint","IMPRINT",EDGE,{"derivedFrom":sQuery(id+"F0.wireOp",EDGE,"E148")}),-1.0]])]});
            var Q4;
            Q4=makeQuery(id+"F0.imprint","IMPRINT",FACE,{"disambiguationData":[TD([[makeQuery(id+"F0.imprint","IMPRINT",EDGE,{"derivedFrom":sQuery(id+"F0.wireOp",EDGE,"E189")}),-1.0]])]});
            var Q5;
            Q5=makeQuery(id+"F0.imprint","IMPRINT",FACE,{"disambiguationData":[TD([[makeQuery(id+"F0.imprint","IMPRINT",EDGE,{"derivedFrom":sQuery(id+"F0.wireOp",EDGE,"E197")}),-1.0]])]});
            var Q6;
            Q6=makeQuery(id+"F0.imprint","IMPRINT",FACE,{"disambiguationData":[TD([[makeQuery(id+"F0.imprint","IMPRINT",EDGE,{"derivedFrom":sQuery(id+"F0.wireOp",EDGE,"E173")}),-1.0]])]});
            var Q7;
            Q7=makeQuery(id+"F0.imprint","IMPRINT",FACE,{"disambiguationData":[TD([[makeQuery(id+"F0.imprint","IMPRINT",EDGE,{"derivedFrom":sQuery(id+"F0.wireOp",EDGE,"E165")}),-1.0]])]});
            var Q8;
            Q8=makeQuery(id+"F0.imprint","IMPRINT",FACE,{"disambiguationData":[TD([[makeQuery(id+"F0.imprint","IMPRINT",EDGE,{"derivedFrom":sQuery(id+"F0.wireOp",EDGE,"E210")}),-1.0]])]});
            var Q9;
            Q9=makeQuery(id+"F0.imprint","IMPRINT",FACE,{"disambiguationData":[TD([[makeQuery(id+"F0.imprint","IMPRINT",EDGE,{"derivedFrom":sQuery(id+"F0.wireOp",EDGE,"E181")}),-1.0]])]});
            var Q10;
            Q10=makeQuery(id+"F0.imprint","IMPRINT",FACE,{"disambiguationData":[TD([[makeQuery(id+"F0.imprint","IMPRINT",EDGE,{"derivedFrom":sQuery(id+"F0.wireOp",EDGE,"E158")}),-1.0]])]});
            var Q11;
            Q11=makeQuery(id+"F0.imprint","IMPRINT",FACE,{"disambiguationData":[TD([[makeQuery(id+"F0.imprint","IMPRINT",EDGE,{"derivedFrom":sQuery(id+"F0.wireOp",EDGE,"E202")}),-1.0]])]});
            var Q12;
            Q12=makeQuery(id+"F0.imprint","IMPRINT",FACE,{"disambiguationData":[TD([[makeQuery(id+"F0.imprint","IMPRINT",EDGE,{"derivedFrom":sQuery(id+"F0.wireOp",EDGE,"E217")}),-1.0]])]});
            extrude(context, id + "F1", {"entities" : qUnion([Q0, Q1, Q2, Q3, Q4, Q5, Q6, Q7, Q8, Q9, Q10, Q11, Q12]), "depth" : 6.35 * mm, "offsetDistance" : 25.4 * mm});
        }
    });
